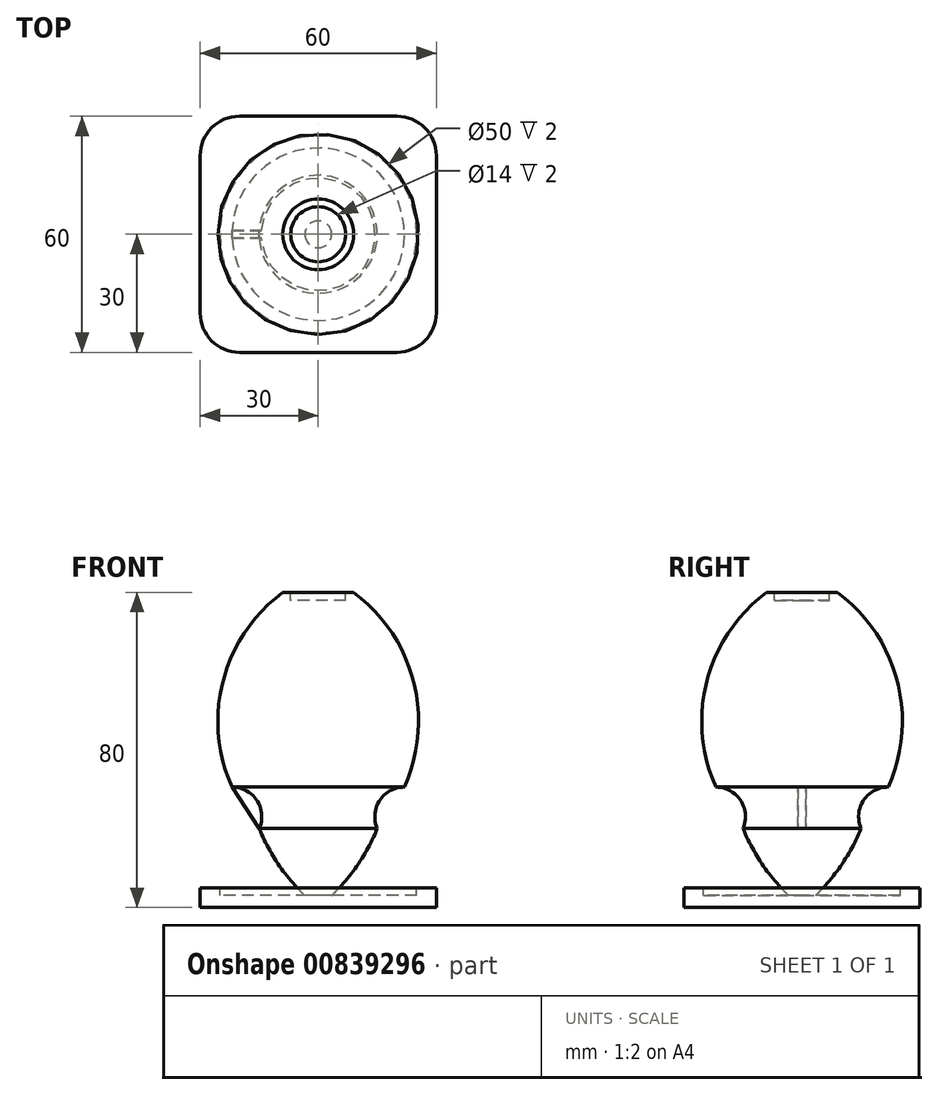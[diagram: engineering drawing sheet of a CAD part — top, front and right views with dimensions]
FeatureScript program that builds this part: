
annotation { "Feature Type Name" : "Feature", "Feature Type Description" : "" }
export const myFeature = defineFeature(function(context is Context, id is Id, definition is map)
    precondition{}
    {
        {
            var Q0;
            Q0=qCreatedBy(makeId("Top.planeOp"),FACE);
            var sketch = newSketch(context, id + "F0", { "sketchPlane" : qUnion([Q0])});
            skLineSegment(sketch, "E0.bottom", {"start": v(30, 30) * mm, "end": v(-30, 30) * mm});
            skLineSegment(sketch, "E0.top", {"start": v(30, -30) * mm, "end": v(-30, -30) * mm});
            skLineSegment(sketch, "E0.left", {"start": v(30, 30) * mm, "end": v(30, -30) * mm});
            skLineSegment(sketch, "E0.right", {"start": v(-30, 30) * mm, "end": v(-30, -30) * mm});
            skPoint(sketch, "E0.middle", {"position": v(0, 0) * mm});
            skSolve(sketch);
        }
        {
            var Q0;
            Q0=makeQuery(id+"F0.imprint","IMPRINT",FACE,{"disambiguationData":[TD([[makeQuery(id+"F0.imprint","IMPRINT",EDGE,{"derivedFrom":sQuery(id+"F0.wireOp",EDGE,"E0.bottom")}),1.0]])]});
            extrude(context, id + "F1", {"entities" : qUnion([Q0]), "depth" : 5 * mm, "offsetDistance" : 25 * mm});
        }
        {
            var Q0;
            Q0=makeQuery(id+"F1.opExtrude","CAP_FACE",FACE,{"disambiguationData":[OSD([sQuery(id+"F0.wireOp",EDGE,"E0.bottom"),sQuery(id+"F0.wireOp",EDGE,"E0.top"),sQuery(id+"F0.wireOp",EDGE,"E0.left"),sQuery(id+"F0.wireOp",EDGE,"E0.right")])],"isStart":false});
            var sketch = newSketch(context, id + "F2", { "sketchPlane" : qUnion([Q0])});
            skCircle(sketch, "E1", {"center": v(0, 0) * mm, "radius": 25 * mm});
            skSolve(sketch);
        }
        {
            var Q0;
            Q0 = qSketchRegion(id + "F2", true);
            extrude(context, id + "F3", {"entities" : qUnion([Q0]), "operationType" : NewBodyOperationType.REMOVE, "oppositeDirection" : true, "depth" : 2 * mm, "offsetDistance" : 25 * mm});
        }
        {
            var Q0;
            Q0=makeQuery(id+"F1.opExtrude","SWEPT_EDGE",EDGE,{"disambiguationData":[OSD([sQuery(id+"F0.wireOp",EDGE,"E0.bottom"),sQuery(id+"F0.wireOp",EDGE,"E0.left")])]});
            var Q1;
            Q1=makeQuery(id+"F1.opExtrude","SWEPT_EDGE",EDGE,{"disambiguationData":[OSD([sQuery(id+"F0.wireOp",EDGE,"E0.bottom"),sQuery(id+"F0.wireOp",EDGE,"E0.right")])]});
            var Q2;
            Q2=makeQuery(id+"F1.opExtrude","SWEPT_EDGE",EDGE,{"disambiguationData":[OSD([sQuery(id+"F0.wireOp",EDGE,"E0.top"),sQuery(id+"F0.wireOp",EDGE,"E0.left")])]});
            var Q3;
            Q3=makeQuery(id+"F1.opExtrude","SWEPT_EDGE",EDGE,{"disambiguationData":[OSD([sQuery(id+"F0.wireOp",EDGE,"E0.top"),sQuery(id+"F0.wireOp",EDGE,"E0.right")])]});
            fillet(context, id + "F4", {"entities" : qUnion([Q0, Q1, Q2, Q3]), "radius" : 10 * mm, "tangentPropagation" : true, "allowEdgeOverflow" : false});
        }
        {
            var Q0;
            Q0=qCreatedBy(makeId("Front.planeOp"),FACE);
            var sketch = newSketch(context, id + "F5", { "sketchPlane" : qUnion([Q0])});
            skLineSegment(sketch, "E2", {"start": v(0, 80) * mm, "end": v(0, 0) * mm});
            skLineSegment(sketch, "E3", {"start": v(0, 80) * mm, "end": v(9, 80) * mm});
            skLineSegment(sketch, "E4", {"start": v(0, 20) * mm, "end": v(15, 20) * mm});
            skLineSegment(sketch, "E5", {"start": v(0, 30.54) * mm, "end": v(21.9, 30.54) * mm});
            skArc(sketch, "E6", {"start": v(21.9, 30.54) * mm, "mid": v(24.18, 57.55) * mm, "end": v(9, 80) * mm});
            skArc(sketch, "E7", {"start": v(21.9, 30.54) * mm, "mid": v(15.6, 27.13) * mm, "end": v(15, 20) * mm});
            skArc(sketch, "E8", {"start": v(0, 0) * mm, "mid": v(8.77, 9.05) * mm, "end": v(15, 20) * mm});
            skLineSegment(sketch, "E9.bottom", {"start": v(0, 80) * mm, "end": v(7, 80) * mm});
            skLineSegment(sketch, "E9.top", {"start": v(0, 78) * mm, "end": v(7, 78) * mm});
            skLineSegment(sketch, "E9.left", {"start": v(0, 80) * mm, "end": v(0, 78) * mm});
            skLineSegment(sketch, "E9.right", {"start": v(7, 80) * mm, "end": v(7, 78) * mm});
            skSolve(sketch);
        }
        {
            var Q0;
            {var subQ0=sQuery(id+"F5.wireOp",EDGE,"E4");Q0=makeQuery(id+"F5.imprint","IMPRINT",FACE,{"disambiguationData":[TD([[makeQuery(id+"F5.imprint","IMPRINT",EDGE,{"derivedFrom":subQ0}),-1.0]])]});}
            var Q1;
            {var subQ0=sQuery(id+"F5.wireOp",EDGE,"E4");Q1=makeQuery(id+"F5.imprint","IMPRINT",FACE,{"disambiguationData":[TD([[makeQuery(id+"F5.imprint","IMPRINT",EDGE,{"derivedFrom":subQ0}),1.0]])]});}
            var Q2;
            {var subQ1=sQuery(id+"F5.wireOp",EDGE,"E5");Q2=makeQuery(id+"F5.imprint","IMPRINT",FACE,{"disambiguationData":[TD([[makeQuery(id+"F5.imprint","IMPRINT",EDGE,{"derivedFrom":subQ1}),1.0]])]});}
            var Q3;
            Q3=sQuery(id+"F5.wireOp",EDGE,"E2");
            revolve(context, id + "F6", {"operationType" : NewBodyOperationType.ADD, "surfaceOperationType" : NewSurfaceOperationType.NEW, "entities" : qUnion([Q0, Q1, Q2]), "axis" : qUnion([Q3]), "revolveType" : RevolveType.FULL});
        }
        {
            var Q0;
            Q0=qCreatedBy(makeId("Front.planeOp"),FACE);
            var sketch = newSketch(context, id + "F7", { "sketchPlane" : qUnion([Q0])});
            skLineSegment(sketch, "E10.0", {"start": v(-15, 20) * mm, "end": v(15, 20) * mm});
            skLineSegment(sketch, "E11.0", {"start": v(-21.9, 30.54) * mm, "end": v(21.9, 30.54) * mm});
            skLineSegment(sketch, "E12", {"start": v(-21.9, 30.54) * mm, "end": v(-15, 20) * mm});
            skLineSegment(sketch, "E13", {"start": v(15, 20) * mm, "end": v(21.9, 30.54) * mm});
            skLineSegment(sketch, "E14", {"start": v(0, 30.54) * mm, "end": v(0, 20) * mm});
            skSolve(sketch);
        }
        {
            var Q0;
            {var subQ0=sQuery(id+"F7.wireOp",EDGE,"E12");Q0=makeQuery(id+"F7.imprint","IMPRINT",FACE,{"disambiguationData":[TD([[makeQuery(id+"F7.imprint","IMPRINT",EDGE,{"derivedFrom":subQ0}),1.0]])]});}
            extrude(context, id + "F8", {"entities" : qUnion([Q0]), "operationType" : NewBodyOperationType.ADD, "endBound" : BoundingType.SYMMETRIC, "depth" : 2 * mm, "offsetDistance" : 25 * mm});
        }
    });
